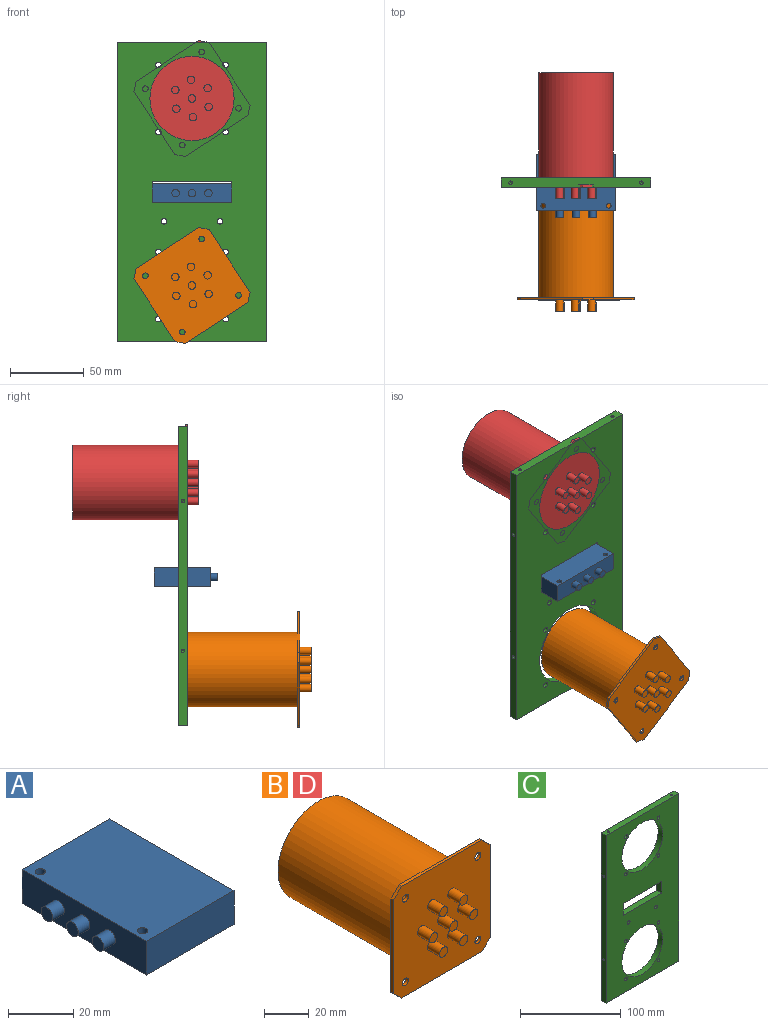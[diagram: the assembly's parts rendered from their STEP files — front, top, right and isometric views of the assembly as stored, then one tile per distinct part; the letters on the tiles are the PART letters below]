
ASSEMBLY  parts=4 mates=3
PART A: 14 faces, bbox 43.2x54x12.7 mm
  f0: plane 53.98x38.1mm, normal (0,0,1), area 2040.6mm2, adj f2,f3,f4,f5,f12,f13
  f1: plane 53.98x38.1mm, normal (0,0,-1), area 2040.6mm2, adj f2,f3,f4,f5,f12,f13
  f2: plane 53.98x12.7mm, normal (-1,0,0), area 624.7mm2, adj f0,f1,f3,f5,f6,f8,f10
  f3: plane 38.1x12.7mm, normal (0,-1,0), area 483.9mm2, adj f0,f1,f2,f4
  f4: plane 53.98x12.7mm, normal (1,0,0), area 685.5mm2, adj f0,f1,f3,f5
  f5: plane 38.1x12.7mm, normal (0,1,0), area 483.9mm2, adj f0,f1,f2,f4
  f6: cylinder r=2.54mm len=5.08mm, axis (1,0,0), area 81.1mm2, adj f2,f7
  f7: plane 5.08x5.08mm, normal (-1,0,0), area 20.3mm2, adj f6
  f8: cylinder r=2.54mm len=5.08mm, axis (1,0,0), area 81.1mm2, adj f2,f9
  f9: plane 5.08x5.08mm, normal (-1,0,0), area 20.3mm2, adj f8
  f10: cylinder r=2.54mm len=5.08mm, axis (1,0,0), area 81.1mm2, adj f2,f11
  f11: plane 5.08x5.08mm, normal (-1,0,0), area 20.3mm2, adj f10
  f12: cylinder r=1.59mm len=12.7mm, axis (0,0,1), area 126.7mm2, adj f0,f1
  f13: cylinder r=1.59mm len=12.7mm, axis (0,0,1), area 126.7mm2, adj f0,f1
PART B: 30 faces, bbox 61x85.4x61 mm
  f0: plane 60.96x60.96mm, normal (0,-1,0), area 3477mm2, adj f4,f5,f6,f7,f8,f9,f10,f11
  f1: plane 60.96x60.96mm, normal (0,1,0), area 1592.1mm2, adj f2,f4,f5,f6,f7,f8,f9,f10
  f2: cylinder r=25.4mm len=76.2mm, axis (0,1,0), area 12161mm2, adj f1,f3
  f3: plane 50.8x50.8mm, normal (0,1,0), area 2026.8mm2, adj f2
  f4: plane 50.8x1.59mm, normal (0,0,1), area 80.6mm2, adj f0,f1,f9,f11
  f5: plane 50.8x1.59mm, normal (-1,0,0), area 80.6mm2, adj f0,f1,f8,f9
  f6: plane 50.8x1.59mm, normal (0,0,-1), area 80.6mm2, adj f0,f1,f8,f10
  f7: plane 50.8x1.59mm, normal (1,0,0), area 80.6mm2, adj f0,f1,f10,f11
  f8: plane 5.08x5.08mm, normal (-0.71,0,-0.71), area 11.4mm2, adj f0,f1,f5,f6
  f9: plane 5.08x5.08mm, normal (-0.71,0,0.71), area 11.4mm2, adj f0,f1,f4,f5
  f10: plane 5.08x5.08mm, normal (0.71,0,-0.71), area 11.4mm2, adj f0,f1,f6,f7
  f11: plane 5.08x5.08mm, normal (0.71,0,0.71), area 11.4mm2, adj f0,f1,f4,f7
  f12: cylinder r=2.54mm len=7.62mm, axis (0,1,0), area 121.6mm2, adj f0,f13
  f13: plane 5.08x5.08mm, normal (0,-1,0), area 20.3mm2, adj f12
  f14: cylinder r=2.54mm len=7.62mm, axis (0,1,0), area 121.6mm2, adj f0,f15
  f15: plane 5.08x5.08mm, normal (0,-1,0), area 20.3mm2, adj f14
  f16: cylinder r=2.54mm len=7.62mm, axis (0,1,0), area 121.6mm2, adj f0,f17
  f17: plane 5.08x5.08mm, normal (0,-1,0), area 20.3mm2, adj f16
  f18: cylinder r=2.54mm len=7.62mm, axis (0,1,0), area 121.6mm2, adj f0,f19
  f19: plane 5.08x5.08mm, normal (0,-1,0), area 20.3mm2, adj f18
  f20: cylinder r=2.54mm len=7.62mm, axis (0,1,0), area 121.6mm2, adj f0,f21
  f21: plane 5.08x5.08mm, normal (0,-1,0), area 20.3mm2, adj f20
  f22: cylinder r=2.54mm len=7.62mm, axis (0,1,0), area 121.6mm2, adj f0,f23
  f23: plane 5.08x5.08mm, normal (0,-1,0), area 20.3mm2, adj f22
  f24: cylinder r=2.54mm len=7.62mm, axis (0,1,0), area 121.6mm2, adj f0,f25
  f25: plane 5.08x5.08mm, normal (0,-1,0), area 20.3mm2, adj f24
  f26: cylinder r=1.91mm len=3.81mm, axis (0,-1,0), area 19mm2, adj f0,f1
  f27: cylinder r=1.91mm len=3.81mm, axis (0,-1,0), area 19mm2, adj f0,f1
  f28: cylinder r=1.91mm len=3.81mm, axis (0,-1,0), area 19mm2, adj f0,f1
  f29: cylinder r=1.91mm len=3.81mm, axis (0,-1,0), area 19mm2, adj f0,f1
PART C: 38 faces, bbox 101.6x6.4x203.2 mm
  f0: plane 203.2x101.6mm, normal (0,1,0), area 14629.5mm2, adj f2,f3,f4,f5,f6,f7,f8,f9
  f1: plane 203.2x101.6mm, normal (0,-1,0), area 14629.5mm2, adj f2,f3,f4,f5,f6,f7,f8,f9
  f2: plane 101.6x6.35mm, normal (0,0,-1), area 637.1mm2, adj f0,f1,f20,f21,f35,f37
  f3: plane 101.6x6.35mm, normal (0,0,1), area 637.1mm2, adj f0,f1,f20,f21,f27,f29
  f4: plane 14.29x6.35mm, normal (1,0,0), area 90.7mm2, adj f0,f1,f5,f6
  f5: plane 53.98x6.35mm, normal (0,0,1), area 342.7mm2, adj f0,f1,f4,f7
  f6: plane 53.98x6.35mm, normal (0,0,-1), area 342.7mm2, adj f0,f1,f4,f7
  f7: plane 14.29x6.35mm, normal (-1,0,0), area 90.7mm2, adj f0,f1,f5,f6
  f8: cylinder r=28.57mm len=57.15mm, axis (0,1,0), area 1140.1mm2, adj f0,f1
  f9: cylinder r=28.57mm len=57.15mm, axis (0,1,0), area 1140.1mm2, adj f0,f1
  f10: cylinder r=1.91mm len=6.35mm, axis (0,-1,0), area 76mm2, adj f0,f1
  f11: cylinder r=1.91mm len=6.35mm, axis (0,-1,0), area 76mm2, adj f0,f1
  f12: cylinder r=1.91mm len=6.35mm, axis (0,-1,0), area 76mm2, adj f0,f1
  f13: cylinder r=1.91mm len=6.35mm, axis (0,-1,0), area 76mm2, adj f0,f1
  f14: cylinder r=1.91mm len=6.35mm, axis (0,-1,0), area 76mm2, adj f0,f1
  f15: cylinder r=1.91mm len=6.35mm, axis (0,-1,0), area 76mm2, adj f0,f1
  f16: cylinder r=1.91mm len=6.35mm, axis (0,-1,0), area 76mm2, adj f0,f1
  f17: cylinder r=1.91mm len=6.35mm, axis (0,-1,0), area 76mm2, adj f0,f1
  f18: cylinder r=1.91mm len=6.35mm, axis (0,-1,0), area 76mm2, adj f0,f1
  f19: cylinder r=1.91mm len=6.35mm, axis (0,-1,0), area 76mm2, adj f0,f1
  f20: plane 203.2x6.35mm, normal (1,0,0), area 1282.3mm2, adj f0,f1,f2,f3,f23,f25
  f21: plane 203.2x6.35mm, normal (-1,0,0), area 1282.3mm2, adj f0,f1,f2,f3,f31,f33
  f22: cone r=0mm half-angle=59deg, axis (1,0,0), area 4.7mm2, adj f23
  f23: cylinder r=1.13mm len=5.08mm, axis (1,0,0), area 36.1mm2, adj f20,f22
  f24: cone r=0mm half-angle=59deg, axis (1,0,0), area 4.7mm2, adj f25
  f25: cylinder r=1.13mm len=5.08mm, axis (1,0,0), area 36.1mm2, adj f20,f24
  f26: cone r=0mm half-angle=59deg, axis (0,0,1), area 4.7mm2, adj f27
  f27: cylinder r=1.13mm len=5.08mm, axis (0,0,1), area 36.1mm2, adj f3,f26
  f28: cone r=0mm half-angle=59deg, axis (0,0,1), area 4.7mm2, adj f29
  f29: cylinder r=1.13mm len=5.08mm, axis (0,0,1), area 36.1mm2, adj f3,f28
  f30: cone r=0mm half-angle=59deg, axis (-1,0,0), area 4.7mm2, adj f31
  f31: cylinder r=1.13mm len=5.08mm, axis (-1,0,0), area 36.1mm2, adj f21,f30
  f32: cone r=0mm half-angle=59deg, axis (-1,0,0), area 4.7mm2, adj f33
  f33: cylinder r=1.13mm len=5.08mm, axis (-1,0,0), area 36.1mm2, adj f21,f32
  f34: cone r=0mm half-angle=59deg, axis (0,0,-1), area 4.7mm2, adj f35
  f35: cylinder r=1.13mm len=5.08mm, axis (0,0,-1), area 36.1mm2, adj f2,f34
  f36: cone r=0mm half-angle=59deg, axis (0,0,-1), area 4.7mm2, adj f37
  f37: cylinder r=1.13mm len=5.08mm, axis (0,0,-1), area 36.1mm2, adj f2,f36
PART D: same geometry as B
PLACE A rot(axis=(0,0,1),90deg) t=(-31.15,74.25,172.29)mm
PLACE B rot(axis=(0,1,0),146.8deg) t=(-58.14,91.4,115.93)mm
PLACE C t=(-96.24,91.4,77.83)mm
PLACE D rot(axis=(0,1,0),146.8deg) t=(-58.14,167.6,242.93)mm
MATE planar A.f1 <-> C.f5  axis (0,0,-1) through (-58.14,93.42,172.29)mm
MATE cylindrical D.f2 <-> C.f9  axis (0,1,0) through (-58.14,167.6,242.93)mm
MATE cylindrical B.f2 <-> C.f8  axis (0,1,0) through (-58.14,53.3,115.93)mm
